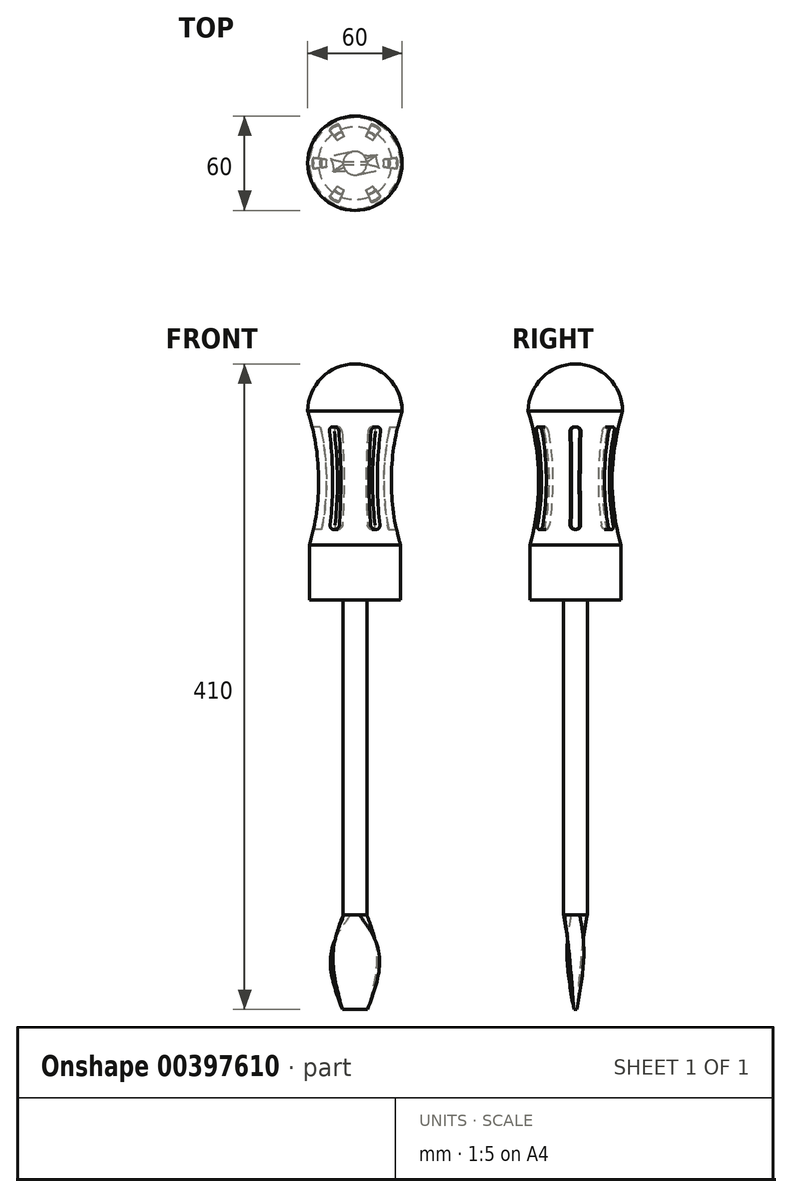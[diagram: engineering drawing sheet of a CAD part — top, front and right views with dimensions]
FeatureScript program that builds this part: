
annotation { "Feature Type Name" : "Feature", "Feature Type Description" : "" }
export const myFeature = defineFeature(function(context is Context, id is Id, definition is map)
    precondition{}
    {
        {
            var Q0;
            Q0=qCreatedBy(makeId("Front.planeOp"),FACE);
            var sketch = newSketch(context, id + "F0", { "sketchPlane" : qUnion([Q0])});
            skLineSegment(sketch, "E0", {"start": v(0, 0) * mm, "end": v(0, 150) * mm});
            skArc(sketch, "E1", {"start": v(0, 150) * mm, "mid": v(21.21, 141.21) * mm, "end": v(30, 120) * mm});
            skArc(sketch, "E2", {"start": v(30, 120) * mm, "mid": v(23.32, 77.58) * mm, "end": v(28.93, 35) * mm});
            skLineSegment(sketch, "E3", {"start": v(28.93, 35) * mm, "end": v(28.93, 0) * mm});
            skLineSegment(sketch, "E4", {"start": v(28.93, 0) * mm, "end": v(0, 0) * mm});
            skLineSegment(sketch, "E5", {"start": v(0, -71.21) * mm, "end": v(0, 186.84) * mm, "construction": true});
            skSolve(sketch);
        }
        {
            var Q0;
            Q0=makeQuery(id+"F0.imprint","IMPRINT",FACE,{"disambiguationData":[TD([[makeQuery(id+"F0.imprint","IMPRINT",EDGE,{"derivedFrom":sQuery(id+"F0.wireOp",EDGE,"E0")}),-1.0]])]});
            var Q1;
            Q1=sQuery(id+"F0.wireOp",EDGE,"E5");
            revolve(context, id + "F1", {"entities" : qUnion([Q0]), "axis" : qUnion([Q1]), "revolveType" : RevolveType.FULL});
        }
        {
            var Q0;
            Q0=qCreatedBy(makeId("Front.planeOp"),FACE);
            var sketch = newSketch(context, id + "F2", { "sketchPlane" : qUnion([Q0])});
            skArc(sketch, "E6.0", {"start": v(22.15, 110) * mm, "mid": v(18.32, 77.54) * mm, "end": v(21.38, 45) * mm});
            skArc(sketch, "E7.0", {"start": v(27.28, 110) * mm, "mid": v(23.32, 77.54) * mm, "end": v(26.48, 45) * mm});
            skLineSegment(sketch, "E8", {"start": v(22.15, 110) * mm, "end": v(27.28, 110) * mm});
            skLineSegment(sketch, "E9", {"start": v(21.38, 45) * mm, "end": v(26.48, 45) * mm});
            skPoint(sketch, "E10.orphan", {"position": v(28.93, 35) * mm});
            skPoint(sketch, "E11.orphan", {"position": v(30, 120) * mm});
            skLineSegment(sketch, "E12", {"start": v(0, -71.06) * mm, "end": v(0, 197.01) * mm, "construction": true});
            skSolve(sketch);
        }
        {
            var Q0;
            Q0=makeQuery(id+"F2.imprint","IMPRINT",FACE,{"disambiguationData":[TD([[makeQuery(id+"F2.imprint","IMPRINT",EDGE,{"derivedFrom":sQuery(id+"F2.wireOp",EDGE,"E6.0")}),1.0]])]});
            var Q1;
            Q1=sQuery(id+"F2.wireOp",EDGE,"E12");
            revolve(context, id + "F3", {"operationType" : NewBodyOperationType.REMOVE, "entities" : qUnion([Q0]), "axis" : qUnion([Q1]), "revolveType" : RevolveType.SYMMETRIC, "oppositeDirection" : true, "angle" : 15 * degree});
        }
        {
            var Q0;
            Q0=makeQuery(id+"F3.boolean.opBoolean","COPY",EDGE,{"derivedFrom":makeQuery(id+"F3.opRevolve","CAP_EDGE",EDGE,{"disambiguationData":[OSD([sQuery(id+"F2.wireOp",EDGE,"E8")])],"isStart":false})});
            var Q1;
            Q1=makeQuery(id+"F3.boolean.opBoolean","COPY",EDGE,{"derivedFrom":makeQuery(id+"F3.opRevolve","CAP_EDGE",EDGE,{"disambiguationData":[OSD([sQuery(id+"F2.wireOp",EDGE,"E8")])],"isStart":true})});
            var Q2;
            Q2=makeQuery(id+"F3.boolean.opBoolean","COPY",EDGE,{"derivedFrom":makeQuery(id+"F3.opRevolve","CAP_EDGE",EDGE,{"disambiguationData":[OSD([sQuery(id+"F2.wireOp",EDGE,"E9")])],"isStart":false})});
            var Q3;
            Q3=makeQuery(id+"F3.boolean.opBoolean","COPY",EDGE,{"derivedFrom":makeQuery(id+"F3.opRevolve","CAP_EDGE",EDGE,{"disambiguationData":[OSD([sQuery(id+"F2.wireOp",EDGE,"E9")])],"isStart":true})});
            fillet(context, id + "F4", {"entities" : qUnion([Q0, Q1, Q2, Q3]), "radius" : 2.8 * mm, "tangentPropagation" : true, "allowEdgeOverflow" : false});
        }
        {
            var Q0;
            Q0=makeQuery(id+"F1.opRevolve","SWEPT_BODY",BODY,{"disambiguationData":[OSD([sQuery(id+"F0.wireOp",EDGE,"E0"),sQuery(id+"F0.wireOp",EDGE,"E1"),sQuery(id+"F0.wireOp",EDGE,"E2"),sQuery(id+"F0.wireOp",EDGE,"E3"),sQuery(id+"F0.wireOp",EDGE,"E4")])]});
            var Q1;
            Q1=makeQuery(id+"F3.boolean.opBoolean","COPY",FACE,{"derivedFrom":makeQuery(id+"F3.opRevolve","CAP_FACE",FACE,{"disambiguationData":[OSD([sQuery(id+"F2.wireOp",EDGE,"E6.0"),sQuery(id+"F2.wireOp",EDGE,"E7.0"),sQuery(id+"F2.wireOp",EDGE,"E8"),sQuery(id+"F2.wireOp",EDGE,"E9")])],"isStart":false})});
            var Q2;
            {var subQ0=sQuery(id+"F2.wireOp",EDGE,"E8");Q2=makeQuery(id+"F4.opFillet","BLEND_FACE",FACE,{"disambiguationData":[OSD([subQ0]),TDD([makeQuery(id+"F3.boolean.opBoolean","COPY",EDGE,{"derivedFrom":makeQuery(id+"F3.opRevolve","CAP_EDGE",EDGE,{"disambiguationData":[OSD([subQ0])],"isStart":false})})])]});}
            var Q3;
            Q3=makeQuery(id+"F3.boolean.opBoolean","COPY",FACE,{"derivedFrom":makeQuery(id+"F3.opRevolve","SWEPT_FACE",FACE,{"disambiguationData":[OSD([sQuery(id+"F2.wireOp",EDGE,"E8")])]})});
            var Q4;
            {var subQ0=sQuery(id+"F2.wireOp",EDGE,"E8");Q4=makeQuery(id+"F4.opFillet","BLEND_FACE",FACE,{"disambiguationData":[OSD([subQ0]),TDD([makeQuery(id+"F3.boolean.opBoolean","COPY",EDGE,{"derivedFrom":makeQuery(id+"F3.opRevolve","CAP_EDGE",EDGE,{"disambiguationData":[OSD([subQ0])],"isStart":true})})])]});}
            var Q5;
            Q5=makeQuery(id+"F3.boolean.opBoolean","COPY",FACE,{"derivedFrom":makeQuery(id+"F3.opRevolve","CAP_FACE",FACE,{"disambiguationData":[OSD([sQuery(id+"F2.wireOp",EDGE,"E6.0"),sQuery(id+"F2.wireOp",EDGE,"E7.0"),sQuery(id+"F2.wireOp",EDGE,"E8"),sQuery(id+"F2.wireOp",EDGE,"E9")])],"isStart":true})});
            var Q6;
            Q6=makeQuery(id+"F3.boolean.opBoolean","COPY",FACE,{"derivedFrom":makeQuery(id+"F3.opRevolve","SWEPT_FACE",FACE,{"disambiguationData":[OSD([sQuery(id+"F2.wireOp",EDGE,"E6.0")])]})});
            var Q7;
            {var subQ0=sQuery(id+"F2.wireOp",EDGE,"E9");Q7=makeQuery(id+"F4.opFillet","BLEND_FACE",FACE,{"disambiguationData":[OSD([subQ0]),TDD([makeQuery(id+"F3.boolean.opBoolean","COPY",EDGE,{"derivedFrom":makeQuery(id+"F3.opRevolve","CAP_EDGE",EDGE,{"disambiguationData":[OSD([subQ0])],"isStart":false})})])]});}
            var Q8;
            Q8=makeQuery(id+"F3.boolean.opBoolean","COPY",FACE,{"derivedFrom":makeQuery(id+"F3.opRevolve","SWEPT_FACE",FACE,{"disambiguationData":[OSD([sQuery(id+"F2.wireOp",EDGE,"E9")])]})});
            var Q9;
            {var subQ0=sQuery(id+"F2.wireOp",EDGE,"E9");Q9=makeQuery(id+"F4.opFillet","BLEND_FACE",FACE,{"disambiguationData":[OSD([subQ0]),TDD([makeQuery(id+"F3.boolean.opBoolean","COPY",EDGE,{"derivedFrom":makeQuery(id+"F3.opRevolve","CAP_EDGE",EDGE,{"disambiguationData":[OSD([subQ0])],"isStart":true})})])]});}
            var Q10;
            Q10=sQuery(id+"F0.wireOp",EDGE,"E5");
            circularPattern(context, id + "F5", {"patternType" : PatternType.FACE, "faces" : qUnion([Q1, Q2, Q3, Q4, Q5, Q6, Q7, Q8, Q9]), "axis" : qUnion([Q10]), "angle" : 360 * degree, "instanceCount" : 6, "equalSpace" : true});
        }
        {
            var Q0;
            Q0=makeQuery(id+"F1.opRevolve","SWEPT_FACE",FACE,{"disambiguationData":[OSD([sQuery(id+"F0.wireOp",EDGE,"E4")])]});
            var sketch = newSketch(context, id + "F6", { "sketchPlane" : qUnion([Q0])});
            skCircle(sketch, "E13", {"center": v(0, 0) * mm, "radius": 7.5 * mm});
            skSolve(sketch);
        }
        {
            var Q0;
            Q0=makeQuery(id+"F6.imprint","IMPRINT",FACE,{"disambiguationData":[TD([[makeQuery(id+"F6.imprint","IMPRINT",EDGE,{"derivedFrom":sQuery(id+"F6.wireOp",EDGE,"E13")}),1.0]])]});
            extrude(context, id + "F7", {"entities" : qUnion([Q0]), "operationType" : NewBodyOperationType.ADD, "depth" : 200 * mm});
        }
        {
            var Q0;
            Q0=makeQuery(id+"F7.opExtrude","CAP_FACE",FACE,{"disambiguationData":[OSD([sQuery(id+"F6.wireOp",EDGE,"E13")])],"isStart":false});
            cPlane(context, id + "F8", {"entities" : qUnion([Q0]), "cplaneType" : CPlaneType.OFFSET, "offset" : 15 * mm, "width" : 152.4 * mm, "height" : 152.4 * mm});
        }
        {
            var Q0;
            Q0=qCreatedBy(id+"F8.planeOp",FACE);
            cPlane(context, id + "F9", {"entities" : qUnion([Q0]), "cplaneType" : CPlaneType.OFFSET, "offset" : 45 * mm, "width" : 152.4 * mm, "height" : 152.4 * mm});
        }
        {
            var Q0;
            Q0=qCreatedBy(id+"F8.planeOp",FACE);
            var sketch = newSketch(context, id + "F10", { "sketchPlane" : qUnion([Q0])});
            skLineSegment(sketch, "E14.bottom", {"start": v(12.5, -5) * mm, "end": v(-12.5, -5) * mm});
            skLineSegment(sketch, "E14.top", {"start": v(12.5, 5) * mm, "end": v(-12.5, 5) * mm});
            skLineSegment(sketch, "E14.left", {"start": v(12.5, -5) * mm, "end": v(12.5, 5) * mm});
            skLineSegment(sketch, "E14.right", {"start": v(-12.5, -5) * mm, "end": v(-12.5, 5) * mm});
            skPoint(sketch, "E14.middle", {"position": v(0, 0) * mm});
            skSolve(sketch);
        }
        {
            var Q0;
            Q0=qCreatedBy(id+"F9.planeOp",FACE);
            var sketch = newSketch(context, id + "F11", { "sketchPlane" : qUnion([Q0])});
            skLineSegment(sketch, "E15.bottom", {"start": v(-8, -1) * mm, "end": v(8, -1) * mm});
            skLineSegment(sketch, "E15.top", {"start": v(-8, 1) * mm, "end": v(8, 1) * mm});
            skLineSegment(sketch, "E15.left", {"start": v(-8, -1) * mm, "end": v(-8, 1) * mm});
            skLineSegment(sketch, "E15.right", {"start": v(8, -1) * mm, "end": v(8, 1) * mm});
            skPoint(sketch, "E15.middle", {"position": v(0, 0) * mm});
            skSolve(sketch);
        }
        {
            var Q0;
            Q0=makeQuery(id+"F7.opExtrude","CAP_FACE",FACE,{"disambiguationData":[OSD([sQuery(id+"F6.wireOp",EDGE,"E13")])],"isStart":false});
            var Q1;
            Q1=makeQuery(id+"F10.imprint","IMPRINT",FACE,{"disambiguationData":[TD([[makeQuery(id+"F10.imprint","IMPRINT",EDGE,{"derivedFrom":sQuery(id+"F10.wireOp",EDGE,"E14.bottom")}),-1.0]])]});
            var Q2;
            Q2=makeQuery(id+"F11.imprint","IMPRINT",FACE,{"disambiguationData":[TD([[makeQuery(id+"F11.imprint","IMPRINT",EDGE,{"derivedFrom":sQuery(id+"F11.wireOp",EDGE,"E15.bottom")}),1.0]])]});
            var Q3;
            Q3=makeQuery(id+"F7.opExtrude","CAP_FACE",FACE,{"disambiguationData":[OSD([sQuery(id+"F6.wireOp",EDGE,"E13")])],"isStart":false});
            var Q4;
            Q4=makeQuery(id+"F10.imprint","IMPRINT",FACE,{"disambiguationData":[TD([[makeQuery(id+"F10.imprint","IMPRINT",EDGE,{"derivedFrom":sQuery(id+"F10.wireOp",EDGE,"E14.bottom")}),-1.0]])]});
            var Q5;
            Q5=makeQuery(id+"F11.imprint","IMPRINT",FACE,{"disambiguationData":[TD([[makeQuery(id+"F11.imprint","IMPRINT",EDGE,{"derivedFrom":sQuery(id+"F11.wireOp",EDGE,"E15.bottom")}),1.0]])]});
            loft(context, id + "F12", {"sheetProfilesArray" : [{ "sheetProfileEntities" : qUnion([Q0]) }, { "sheetProfileEntities" : qUnion([Q1]) }, { "sheetProfileEntities" : qUnion([Q2]) }], "wireProfilesArray" : [{ "wireProfileEntities" : qUnion([Q3]) }, { "wireProfileEntities" : qUnion([Q4]) }, { "wireProfileEntities" : qUnion([Q5]) }]});
        }
    });
